# Revit family: rs_10_l_730512
name_source: partatom
category: Leuchten
revit_build: Autodesk Revit 2016 (Build: 20190508_0715(x64)
units: mm (PartAtom-declared; Revit-internal decimal feet)

## family parameters
Basisbauteil = Fläche
Beim Laden mit Abzugskörper schneiden = Nein
Bemaßung runder Anschluss = Durchmesser verwenden
Gemeinsam genutzt = Nein
Lichtquelle = Nein
Raumberechnungspunkt = Nein
Teiletyp = Normal

## types (1)
- RS 10 L (1 x )
    Beschreibung = Dimensions (Ø x H): 280 x 110 mm; Mains power supply: 230 – 240 V / 50 Hz; Sensor Technology: High frequency; Transmitter power: < 1 mW; HF-system: 5,8 GHz; Output: 75 W; Interconnection: Yes; Switching output 1, resistive: 800 W; Type of interconnection: Master/master; With lamp: No; Lamp: All-purpose lamp; Base: E27; With motion detector: Yes; Detection: also through glass, wood and stud walls; Detection angle: 360 °; Angle of aperture: 160 °; Capability of masking out individual segments: No; Electronic scalability: Yes; Mechanical scalability: No; Reach, radial: Ø 8 m (50 m²); Reach, tangential: Ø 8 m (50 m²); Continuous light: selectable; Photo-cell controller: Yes; Twilight setting: 2 – 2000 lx; Time setting: 5 sec – 15 min; Basic light level function: No; Soft light start: No; Impact resistance: IK03; IP-rating: IP44; Protection class: II; Ambient temperature: -20 – 40 °C; Housing material: Plastic; Cover material: Glass opal; Manufacturer's Warranty: 5 years; Settings via: Potentiometers; With remote control: No; PU1, EAN: 4007841730512
    CIE Flux Codes = 40 68 88 83 57
    Frequency = 50 Hz
    Height = 0 mm  [stored 0 ft]
    Hersteller = Steinel
    Lamp count = 1
    Lampe = 1 x
    Length = 280 mm
    Luminous efficacy = 0 lm/W
    ModVariant = Nein
    Modell = 730512
    Mounting Type = Surface mounted
    Number of Poles = 1
    OnlyDefault = Ja
    Power Factor = 1
    Product Name = RS 10 L
    Product group = Sensor-switched indoor light
    ProductGroupID = 30
    Protection Class = Protection class II
    Protection Degree = IP 34
    RlxData = <blob elided: 19633 chars, md5=102a5dcb>
    Scheinlast = 75 VA
    Socket = socket
    Standby Power = 0 W
    System Light Flux = 0 lm
    System Power = 75 W
    Typenbild = produkt1_730512.jpg
    Typenkommentare = Product without accessories
    URL = http://relux.com
    VarID = ---
    Voltage = 0 V
    Vorgabe-Ansicht = 1800 mm
    Weight = 0.00 kg
    Width = 0 mm  [stored 0 ft]

note: [stored X ft] marks values corroborated as IEEE doubles in the binary element streams (Revit-internal decimal feet)

## geometry (parser evidence)
native form markers: Blend x4, Sweep x16
no freeform markers — native parametric forms only
